# Revit family: INT-3-K
name_source: partatom
category: Lighting Fixtures
units: mm (PartAtom-declared; Revit-internal decimal feet)

## family parameters
Cut with Voids When Loaded = No
Host = Face
Light Source = No
OmniClass Number = 23.80.70.11.14.17
OmniClass Title = Direct/Indirect
Part Type = Normal
Room Calculation Point = No
Round Connector Dimension = Use Diameter
Shared = Yes

## types (1)
- INT
    Angle Tilt = 45°
    Apparent Load = 15 VA
    Assembly Code = D5020200
    Connector Description = Lighting Connector
    Default Elevation = 48 "
    Description = Intent
    Features = Architectural linear product for wall and ground mounting
applications such as sign lighting, wall washing, wall grazing, and
building accent lighting
• IP66 rated product with linear run capabilities
• Lumen range from 657 to 3,271 lm
    Fixture distribution = Direct
    Glass = Glass
    Height = 4 "
    Housing Material = Paint -  Basic Black Textured
    Lamp = LED
    Length = 24 "
    Load Classification = Lighting
    Manufacturer = Kim Lighting
    Model = INT-3-K
    Mounting = Paint -  Light Silver
    Power Factor = 1
    Reflector Finish = White Glass
    URL = https://www.currentlighting.com
    Voltage = 120 V
    Warranty = 5 years Warranty
    Wattage Comments = 15W
    Watts = 15 W
    Width = 3.875 "
    Wings = Paint -  Light Silver
    zz Angle = 45°

## geometry (parser evidence)
native form markers: Sweep x7
no freeform markers — native parametric forms only
